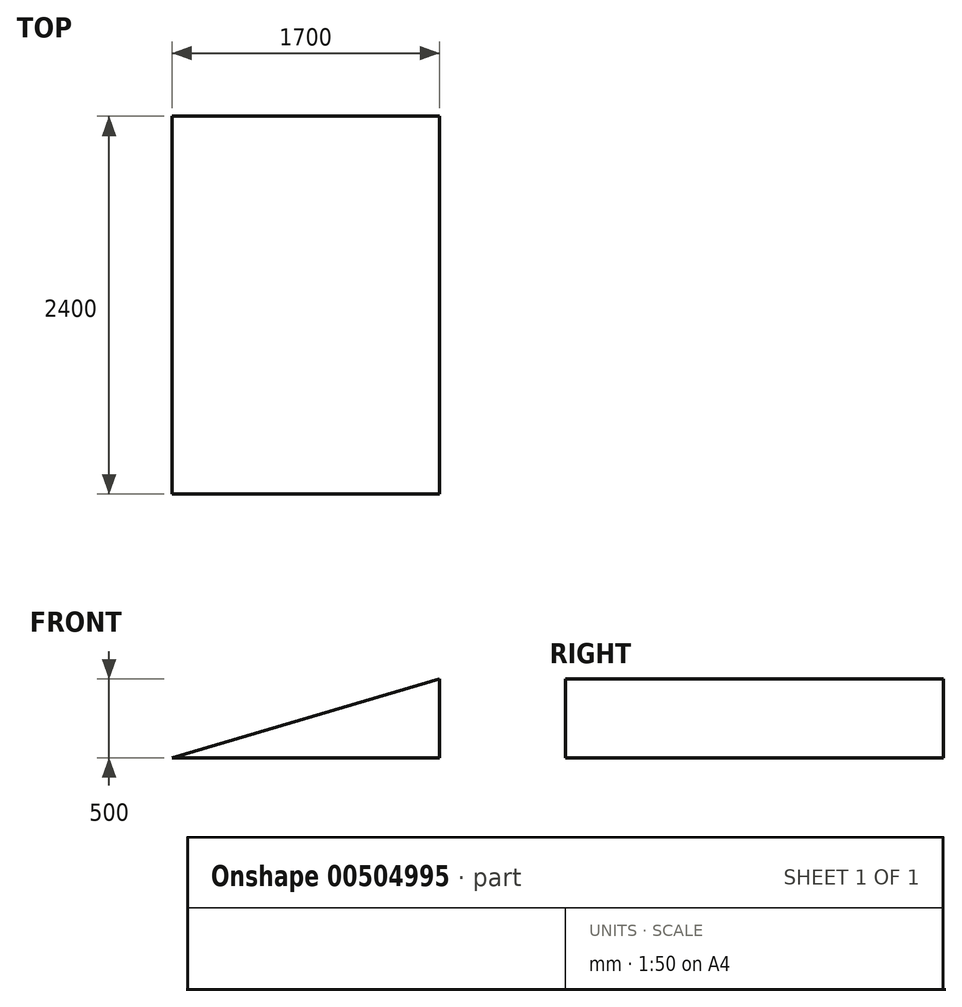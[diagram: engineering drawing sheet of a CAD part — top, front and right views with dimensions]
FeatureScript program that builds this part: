
annotation { "Feature Type Name" : "Feature", "Feature Type Description" : "" }
export const myFeature = defineFeature(function(context is Context, id is Id, definition is map)
    precondition{}
    {
        {
            var Q0;
            Q0=qCreatedBy(makeId("Front.planeOp"),FACE);
            var sketch = newSketch(context, id + "F0", { "sketchPlane" : qUnion([Q0])});
            skLineSegment(sketch, "E0", {"start": v(-884.04, 0) * mm, "end": v(815.96, 500) * mm});
            skLineSegment(sketch, "E1", {"start": v(-884.04, 0) * mm, "end": v(815.96, 0) * mm});
            skLineSegment(sketch, "E2", {"start": v(815.96, 500) * mm, "end": v(815.96, 0) * mm});
            skSolve(sketch);
        }
        {
            var Q0;
            Q0=makeQuery(id+"F0.imprint","IMPRINT",FACE,{"disambiguationData":[TD([[makeQuery(id+"F0.imprint","IMPRINT",EDGE,{"derivedFrom":sQuery(id+"F0.wireOp",EDGE,"E0")}),-1.0]])]});
            extrude(context, id + "F1", {"entities" : qUnion([Q0]), "depth" : 2400 * mm});
        }
    });
